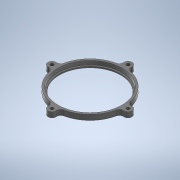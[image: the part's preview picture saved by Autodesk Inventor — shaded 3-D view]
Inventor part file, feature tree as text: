
AUTODESK INVENTOR PART (.ipt)
format: ipt  version: 2020 (Build 240168000, 168)  size: 215,552 bytes
history: native  units: in
note: dims shown in document units (in); Inventor stores cm internally (conversion verified against a paired STEP export)
features: sketch x2, revolve x1, extrude x1, pattern_circular x1, fillet x1
ambient origin geometry x8: Origin, YZ Plane, XZ Plane, XY Plane, X Axis, Y Axis, Z Axis, Center Point
bodies: Solid1 (feature_tree)
feature tree (6):
  revolve  "Revolution1"  [1 undecoded]
  extrude  "Extrusion1"  Depth=0.125in
  pattern_circular  "Circular Pattern1"  [2 undecoded]
  fillet  "Fillet1"  [1 undecoded]
  sketch  "Sketch1"  dims[d0=2.0in d2=0.25in]
  sketch  "Sketch2"  dims[d3=0.1in d4=0.125in d5=0.375in d6=90.0deg d7=0.2031in d9=1.0in d10=0.0in d11=1.5748in d12=360.0deg d14=0.5in d15=0.0625in]
note: 4 required parameter values undecoded (feature->parameter linkage not recoverable at this tier; creation-order binding heuristic only, values carry confidence <= 0.55)